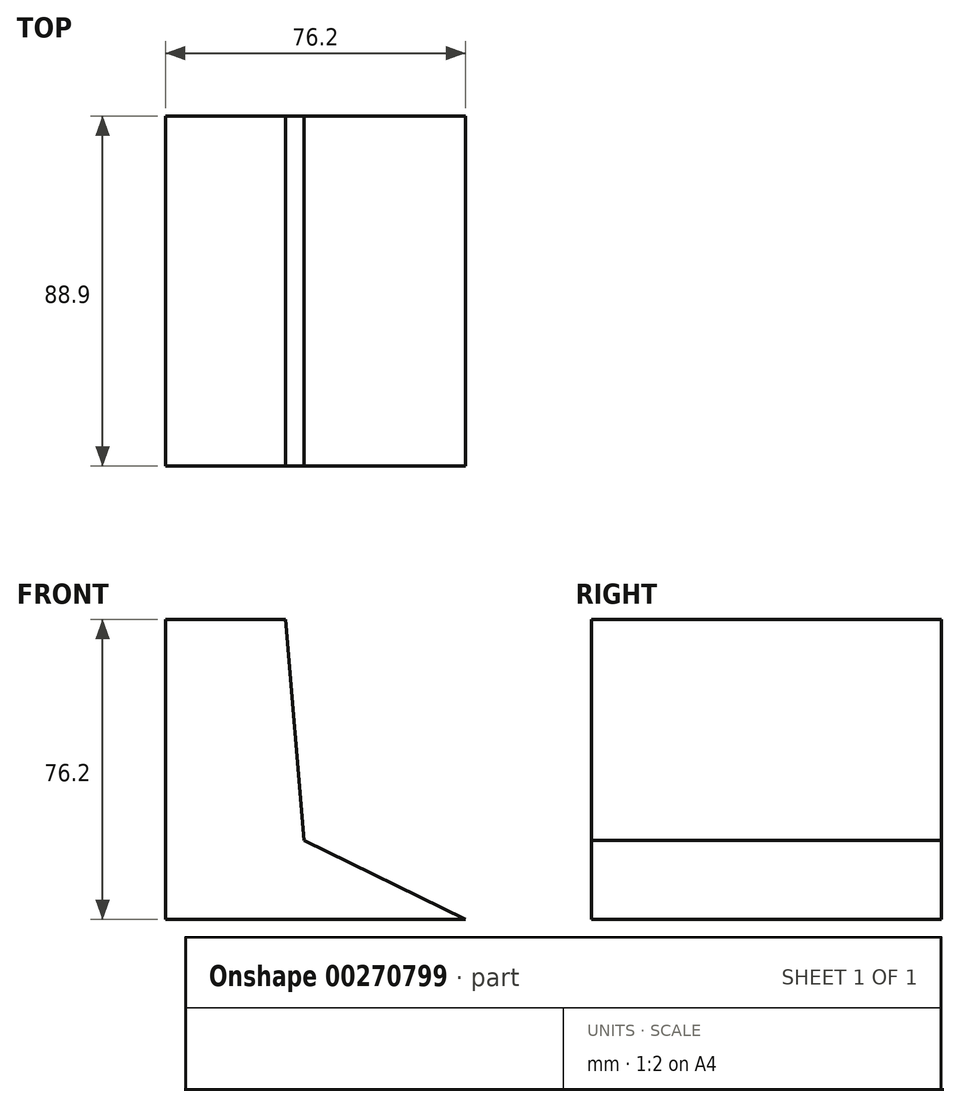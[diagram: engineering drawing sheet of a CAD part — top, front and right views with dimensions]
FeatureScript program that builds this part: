
annotation { "Feature Type Name" : "Feature", "Feature Type Description" : "" }
export const myFeature = defineFeature(function(context is Context, id is Id, definition is map)
    precondition{}
    {
        {
            var Q0;
            Q0=qCreatedBy(makeId("Front.planeOp"),FACE);
            var sketch = newSketch(context, id + "F0", { "sketchPlane" : qUnion([Q0])});
            skLineSegment(sketch, "E0", {"start": v(-52.6, 25.93) * mm, "end": v(-52.6, -50.27) * mm});
            skLineSegment(sketch, "E1", {"start": v(-52.6, -50.27) * mm, "end": v(23.6, -50.27) * mm});
            skLineSegment(sketch, "E2", {"start": v(23.6, -50.27) * mm, "end": v(-17.47, -30.19) * mm});
            skLineSegment(sketch, "E3", {"start": v(-52.6, 25.93) * mm, "end": v(-22.12, 25.93) * mm});
            skLineSegment(sketch, "E4", {"start": v(-22.12, 25.93) * mm, "end": v(-17.47, -30.19) * mm});
            skSolve(sketch);
        }
        {
            var Q0;
            Q0 = qSketchRegion(id + "F0", true);
            extrude(context, id + "F1", {"entities" : qUnion([Q0]), "depth" : 88.9 * mm});
        }
    });
